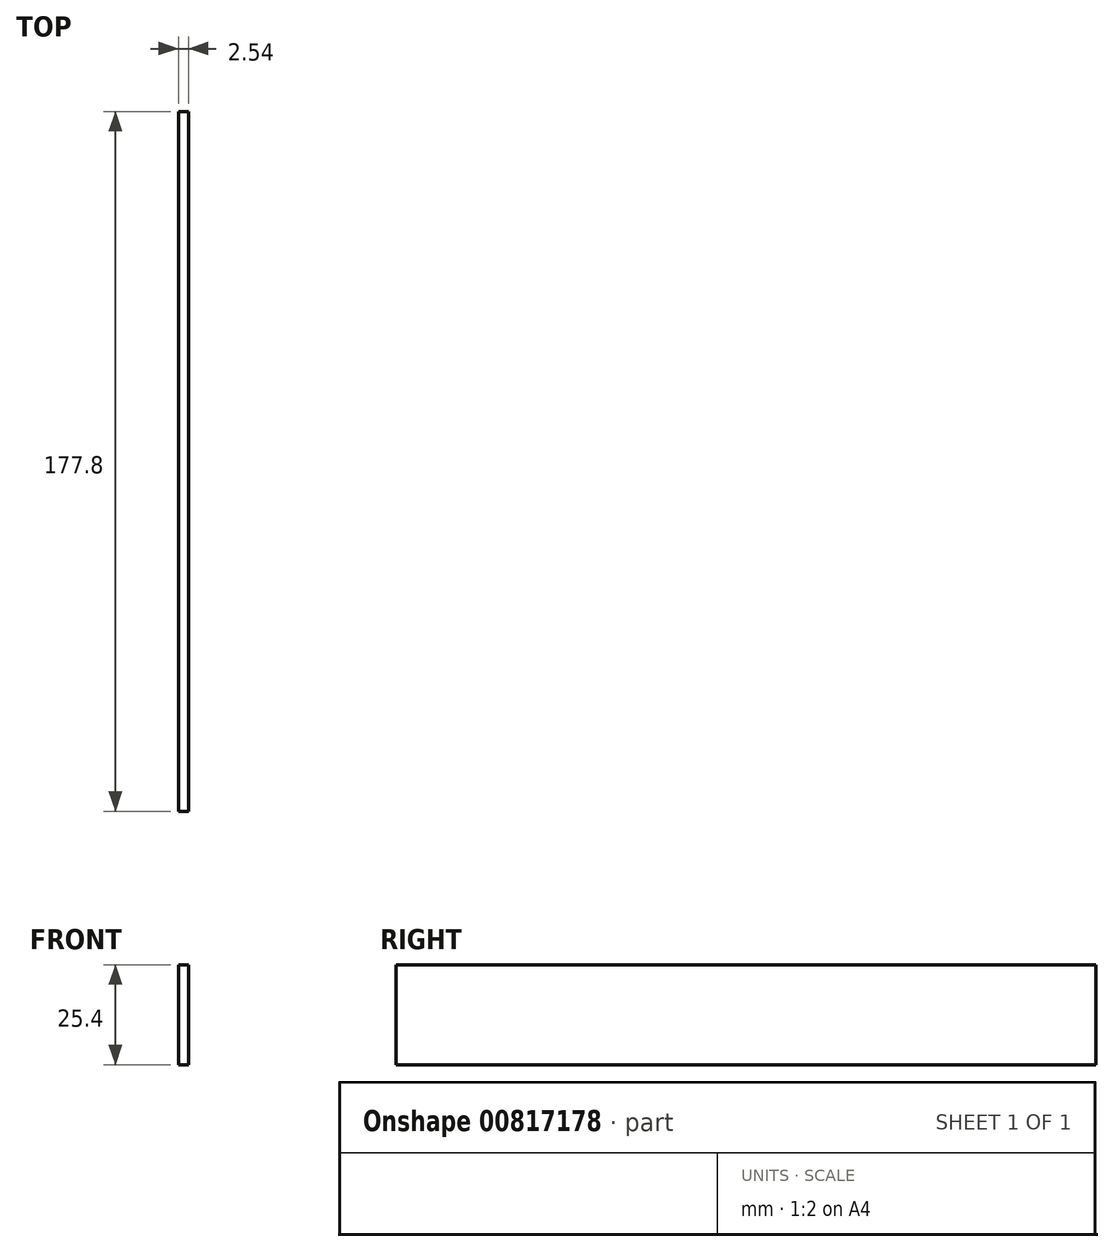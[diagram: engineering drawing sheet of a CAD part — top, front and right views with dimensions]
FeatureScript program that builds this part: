
annotation { "Feature Type Name" : "Feature", "Feature Type Description" : "" }
export const myFeature = defineFeature(function(context is Context, id is Id, definition is map)
    precondition{}
    {
        {
            var Q0;
            Q0=qCreatedBy(makeId("Top.planeOp"),FACE);
            var sketch = newSketch(context, id + "F0", { "sketchPlane" : qUnion([Q0])});
            skLineSegment(sketch, "E0.bottom", {"start": v(-59.94, -70.68) * mm, "end": v(-57.4, -70.68) * mm});
            skLineSegment(sketch, "E0.top", {"start": v(-59.94, 107.12) * mm, "end": v(-57.4, 107.12) * mm});
            skLineSegment(sketch, "E0.left", {"start": v(-59.94, -70.68) * mm, "end": v(-59.94, 107.12) * mm});
            skLineSegment(sketch, "E0.right", {"start": v(-57.4, -70.68) * mm, "end": v(-57.4, 107.12) * mm});
            skSolve(sketch);
        }
        {
            var Q0;
            Q0=makeQuery(id+"F0.imprint","IMPRINT",FACE,{"disambiguationData":[TD([[makeQuery(id+"F0.imprint","IMPRINT",EDGE,{"derivedFrom":sQuery(id+"F0.wireOp",EDGE,"E0.bottom")}),1.0]])]});
            extrude(context, id + "F1", {"entities" : qUnion([Q0]), "depth" : 25.4 * mm, "offsetDistance" : 25.4 * mm});
        }
    });
